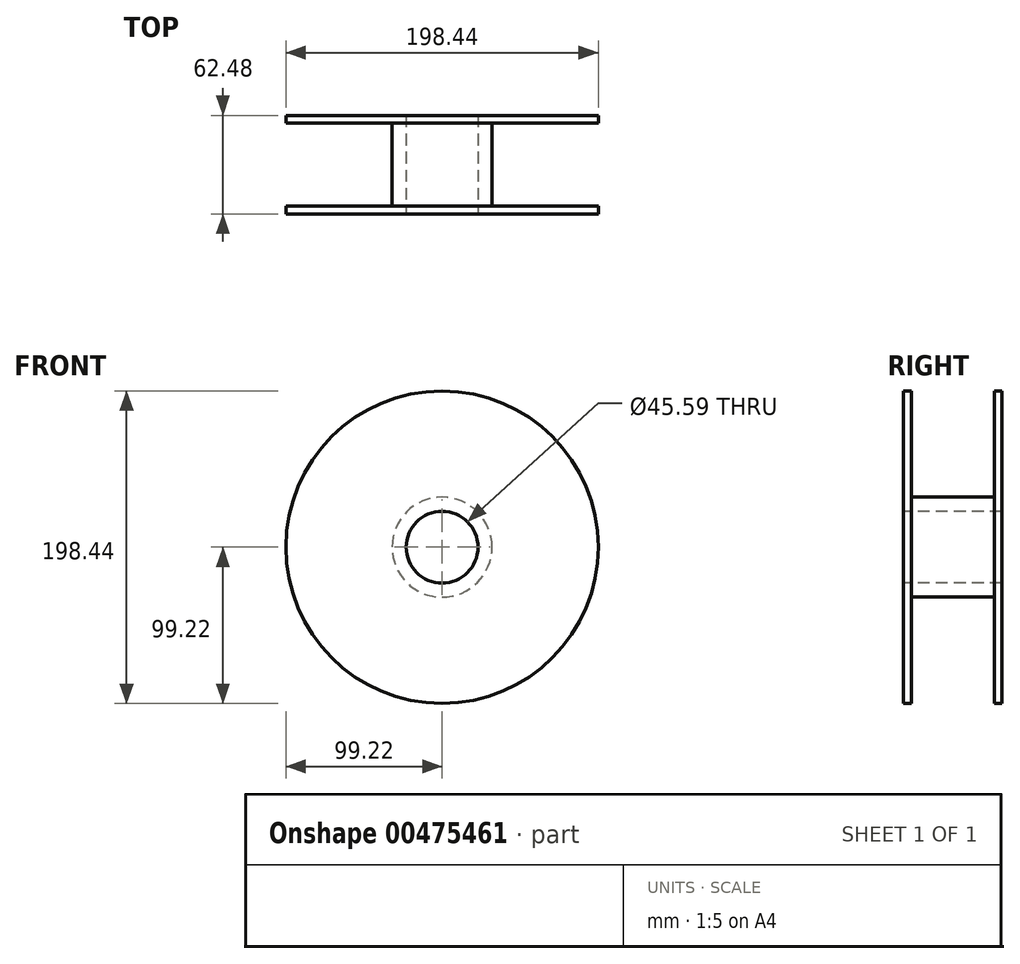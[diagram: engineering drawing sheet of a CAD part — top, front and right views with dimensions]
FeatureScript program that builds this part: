
annotation { "Feature Type Name" : "Feature", "Feature Type Description" : "" }
export const myFeature = defineFeature(function(context is Context, id is Id, definition is map)
    precondition{}
    {
        {
            var Q0;
            Q0=qCreatedBy(makeId("Front.planeOp"),FACE);
            var sketch = newSketch(context, id + "F0", { "sketchPlane" : qUnion([Q0])});
            skCircle(sketch, "E0", {"center": v(0, 0) * mm, "radius": 99.22 * mm});
            skSolve(sketch);
        }
        {
            var Q0;
            Q0 = qSketchRegion(id + "F0", true);
            extrude(context, id + "F1", {"entities" : qUnion([Q0]), "oppositeDirection" : true, "depth" : 4.95 * mm});
        }
        {
            var Q0;
            Q0=qCreatedBy(makeId("Front.planeOp"),FACE);
            cPlane(context, id + "F2", {"entities" : qUnion([Q0]), "cplaneType" : CPlaneType.OFFSET, "offset" : 62.48 * mm, "oppositeDirection" : true, "width" : 152.4 * mm, "height" : 152.4 * mm});
        }
        {
            var Q0;
            Q0=qCreatedBy(id+"F2.planeOp",FACE);
            var sketch = newSketch(context, id + "F3", { "sketchPlane" : qUnion([Q0])});
            skCircle(sketch, "E1", {"center": v(0, 0) * mm, "radius": 99.22 * mm});
            skSolve(sketch);
        }
        {
            var Q0;
            Q0=makeQuery(id+"F1.opExtrude","CAP_FACE",FACE,{"disambiguationData":[OSD([sQuery(id+"F0.wireOp",EDGE,"E0")])],"isStart":true});
            var sketch = newSketch(context, id + "F4", { "sketchPlane" : qUnion([Q0])});
            skCircle(sketch, "E2", {"center": v(0, 0) * mm, "radius": 31.75 * mm});
            skSolve(sketch);
        }
        {
            var Q0;
            Q0 = qSketchRegion(id + "F4", true);
            var Q1;
            Q1=makeQuery(id+"F6.opExtrude","CAP_FACE",FACE,{"disambiguationData":[OSD([sQuery(id+"F3.wireOp",EDGE,"E1")])],"isStart":false});
            extrude(context, id + "F5", {"entities" : qUnion([Q0]), "operationType" : NewBodyOperationType.ADD, "oppositeDirection" : true, "endBoundEntityFace" : qUnion([Q1]), "depth" : 62.23 * mm});
        }
        {
            var Q0;
            Q0 = qSketchRegion(id + "F3", true);
            extrude(context, id + "F6", {"entities" : qUnion([Q0]), "operationType" : NewBodyOperationType.ADD, "depth" : 4.95 * mm});
        }
        {
            var Q0;
            Q0=makeQuery(id+"F1.opExtrude","CAP_FACE",FACE,{"disambiguationData":[OSD([sQuery(id+"F0.wireOp",EDGE,"E0")])],"isStart":true});
            var sketch = newSketch(context, id + "F7", { "sketchPlane" : qUnion([Q0])});
            skCircle(sketch, "E3", {"center": v(0, 0) * mm, "radius": 22.8 * mm});
            skSolve(sketch);
        }
        {
            var Q0;
            Q0 = qSketchRegion(id + "F7", true);
            extrude(context, id + "F8", {"entities" : qUnion([Q0]), "operationType" : NewBodyOperationType.REMOVE, "endBound" : BoundingType.THROUGH_ALL, "oppositeDirection" : true, "depth" : 25.4 * mm});
        }
    });
